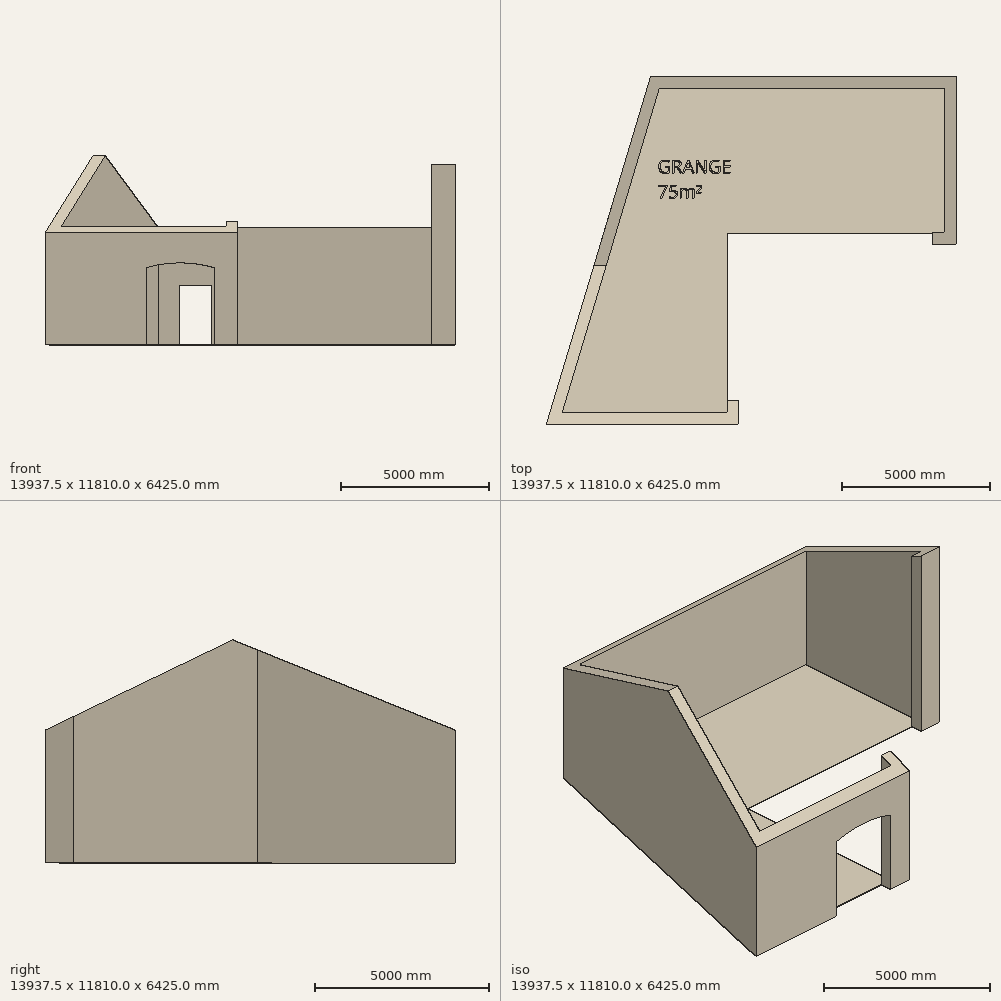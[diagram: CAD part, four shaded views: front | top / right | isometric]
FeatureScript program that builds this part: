
annotation { "Feature Type Name" : "Feature", "Feature Type Description" : "" }
export const myFeature = defineFeature(function(context is Context, id is Id, definition is map)
    precondition{}
    {
        {
            var Q0;
            Q0=qCreatedBy(makeId("Top.planeOp"),FACE);
            var sketch = newSketch(context, id + "F0", { "sketchPlane" : qUnion([Q0])});
            skLineSegment(sketch, "E0", {"start": v(-9700, 4910) * mm, "end": v(0, 4910) * mm});
            skLineSegment(sketch, "E1", {"start": v(-9700, 4910) * mm, "end": v(-13000, -6100) * mm});
            skLineSegment(sketch, "E2", {"start": v(0, 4910) * mm, "end": v(0, 0) * mm});
            skLineSegment(sketch, "E3", {"start": v(-7400, -6100) * mm, "end": v(-13000, -6100) * mm});
            skLineSegment(sketch, "E4.0", {"start": v(-9997.69, 5310) * mm, "end": v(400, 5310) * mm});
            skLineSegment(sketch, "E4.1", {"start": v(-7000, -6500) * mm, "end": v(-13537.47, -6500) * mm});
            skLineSegment(sketch, "E4.3", {"start": v(-9997.69, 5310) * mm, "end": v(-13537.47, -6500) * mm});
            skLineSegment(sketch, "E4.5", {"start": v(400, 5310) * mm, "end": v(400, -400) * mm});
            skLineSegment(sketch, "E5", {"start": v(-7400, -6100) * mm, "end": v(-7400, -5700) * mm});
            skLineSegment(sketch, "E6", {"start": v(-7400, -5700) * mm, "end": v(-7000, -5700) * mm});
            skLineSegment(sketch, "E7", {"start": v(-7000, -5700) * mm, "end": v(-7000, -6500) * mm});
            skLineSegment(sketch, "E8", {"start": v(0, 0) * mm, "end": v(-400, 0) * mm});
            skLineSegment(sketch, "E9", {"start": v(-400, 0) * mm, "end": v(-400, -400) * mm});
            skLineSegment(sketch, "E10", {"start": v(-400, -400) * mm, "end": v(400, -400) * mm});
            skSolve(sketch);
        }
        {
            var Q0;
            Q0 = qSketchRegion(id + "F0", true);
            extrude(context, id + "F1", {"entities" : qUnion([Q0]), "depth" : 6400 * mm});
        }
        {
            var Q0;
            Q0=qCreatedBy(makeId("Right.planeOp"),FACE);
            var sketch = newSketch(context, id + "F2", { "sketchPlane" : qUnion([Q0])});
            skLineSegment(sketch, "E11", {"start": v(-6500, 3800) * mm, "end": v(-1100, 6400) * mm});
            skLineSegment(sketch, "E12", {"start": v(-1100, 6400) * mm, "end": v(5310, 3800) * mm});
            skLineSegment(sketch, "E13", {"start": v(5310, 3800) * mm, "end": v(5310, 0) * mm});
            skLineSegment(sketch, "E14", {"start": v(5310, 3800) * mm, "end": v(5310, 6400) * mm});
            skLineSegment(sketch, "E15", {"start": v(-6500, 6400) * mm, "end": v(5310, 6400) * mm});
            skLineSegment(sketch, "E16", {"start": v(-6500, 6400) * mm, "end": v(-6500, 3800) * mm});
            skSolve(sketch);
        }
        {
            var Q0;
            Q0 = qSketchRegion(id + "F2", true);
            extrude(context, id + "F3", {"entities" : qUnion([Q0]), "operationType" : NewBodyOperationType.REMOVE, "endBound" : BoundingType.THROUGH_ALL, "depth" : 25.4 * mm, "hasSecondDirection" : true, "secondDirectionBound" : BoundingType.THROUGH_ALL, "secondDirectionOppositeDirection" : true, "secondDirectionDepth" : 25.4 * mm});
        }
        {
            var Q0;
            Q0=makeQuery(id+"F1.opExtrude","SWEPT_FACE",FACE,{"disambiguationData":[OSD([sQuery(id+"F0.wireOp",EDGE,"E4.0")])]});
            var sketch = newSketch(context, id + "F4", { "sketchPlane" : qUnion([Q0])});
            skLineSegment(sketch, "E17.bottom", {"start": v(7897.69, 0) * mm, "end": v(8997.69, 0) * mm});
            skLineSegment(sketch, "E17.top", {"start": v(7897.69, 2000) * mm, "end": v(8997.69, 2000) * mm});
            skLineSegment(sketch, "E17.left", {"start": v(7897.69, 0) * mm, "end": v(7897.69, 2000) * mm});
            skLineSegment(sketch, "E17.right", {"start": v(8997.69, 0) * mm, "end": v(8997.69, 2000) * mm});
            skSolve(sketch);
        }
        {
            var Q0;
            Q0 = qSketchRegion(id + "F4", true);
            extrude(context, id + "F5", {"entities" : qUnion([Q0]), "operationType" : NewBodyOperationType.REMOVE, "endBound" : BoundingType.UP_TO_NEXT, "oppositeDirection" : true, "depth" : 25.4 * mm});
        }
        {
            var Q0;
            Q0=makeQuery(id+"F1.opExtrude","SWEPT_FACE",FACE,{"disambiguationData":[OSD([sQuery(id+"F0.wireOp",EDGE,"E4.1")])]});
            var sketch = newSketch(context, id + "F6", { "sketchPlane" : qUnion([Q0])});
            skLineSegment(sketch, "E18", {"start": v(-10100, 0) * mm, "end": v(-10100, 2600) * mm});
            skArc(sketch, "E19", {"start": v(-7800, 2600) * mm, "mid": v(-8950, 2768.88) * mm, "end": v(-10100, 2600) * mm});
            skLineSegment(sketch, "E20", {"start": v(-7800, 2600) * mm, "end": v(-7800, 0) * mm});
            skLineSegment(sketch, "E21", {"start": v(-7800, 0) * mm, "end": v(-10100, 0) * mm});
            skSolve(sketch);
        }
        {
            var Q0;
            Q0 = qSketchRegion(id + "F6", true);
            extrude(context, id + "F7", {"entities" : qUnion([Q0]), "operationType" : NewBodyOperationType.REMOVE, "endBound" : BoundingType.UP_TO_NEXT, "oppositeDirection" : true, "depth" : 25.4 * mm});
        }
        {
            var Q0;
            {var subQ0=sQuery(id+"F0.wireOp",EDGE,"E3");var subQ1=sQuery(id+"F0.wireOp",EDGE,"E4.0");var subQ2=sQuery(id+"F0.wireOp",EDGE,"E1");var subQ3=sQuery(id+"F0.wireOp",EDGE,"E0");var subQ4=sQuery(id+"F0.wireOp",EDGE,"E4.3");var subQ5=sQuery(id+"F0.wireOp",EDGE,"E4.1");Q0=makeQuery(id+"F7.boolean.opBoolean","SPLIT",FACE,{"disambiguationData":[TD([makeQuery(id+"F1.opExtrude","SWEPT_FACE",FACE,{"disambiguationData":[OSD([subQ2])]})])],"derivedFrom":makeQuery(id+"F1.opExtrude","CAP_FACE",FACE,{"disambiguationData":[OSD([subQ3,subQ2,sQuery(id+"F0.wireOp",EDGE,"E2"),sQuery(id+"F0.wireOp",EDGE,"q86xWEi4-8NHh-2lQc-s4JO-oboVVbpXyoTF"),sQuery(id+"F0.wireOp",EDGE,"fW7YdV6a-fR6s-xuWl-E4J9-OQ2L1WpyIvuU"),subQ0,subQ1,subQ5,sQuery(id+"F0.wireOp",EDGE,"E4.2"),subQ4,sQuery(id+"F0.wireOp",EDGE,"E4.4"),sQuery(id+"F0.wireOp",EDGE,"E4.5")])],"isStart":true})});}
            var sketch = newSketch(context, id + "F8", { "sketchPlane" : qUnion([Q0])});
            skLineSegment(sketch, "E22", {"start": v(-9997.69, -5310) * mm, "end": v(400, -5310) * mm});
            skLineSegment(sketch, "E23", {"start": v(400, -5310) * mm, "end": v(400, -5310) * mm});
            skLineSegment(sketch, "E24", {"start": v(-13417.58, 6100) * mm, "end": v(-9997.69, -5310) * mm});
            skLineSegment(sketch, "E25", {"start": v(400, -5310) * mm, "end": v(400, 0) * mm});
            skLineSegment(sketch, "E26", {"start": v(400, 0) * mm, "end": v(-7400, 0) * mm});
            skLineSegment(sketch, "E27", {"start": v(-7400, 0) * mm, "end": v(-7400, 6100) * mm});
            skLineSegment(sketch, "E28", {"start": v(-7400, 6100) * mm, "end": v(-13417.58, 6100) * mm});
            skSolve(sketch);
        }
        {
            var Q0;
            Q0 = qSketchRegion(id + "F8", true);
            extrude(context, id + "F9", {"entities" : qUnion([Q0]), "operationType" : NewBodyOperationType.ADD, "oppositeDirection" : true, "depth" : 1 * mm, "hasSecondDirection" : true, "secondDirectionOppositeDirection" : false, "secondDirectionDepth" : 25 * mm});
        }
        {
            var Q0;
            Q0=makeQuery(id+"F9.opExtrude","CAP_FACE",FACE,{"disambiguationData":[OSD([sQuery(id+"F8.wireOp",EDGE,"E22"),sQuery(id+"F8.wireOp",EDGE,"E24"),sQuery(id+"F8.wireOp",EDGE,"E25"),sQuery(id+"F8.wireOp",EDGE,"E26"),sQuery(id+"F8.wireOp",EDGE,"E27"),sQuery(id+"F8.wireOp",EDGE,"E28")])],"isStart":false});
            var sketch = newSketch(context, id + "F10", { "sketchPlane" : qUnion([Q0])});
            skText(sketch, "E29", { "text": "GRANGE\n75m²", "fontName": "OpenSans-Regular.ttf"});
            const initialGuessF10  = {"E29": [-9.75796, 2.02622, 1, 0, 0.45193]};
            skSetInitialGuess(sketch, initialGuessF10);
            skSolve(sketch);
        }
        {
            var Q0;
            Q0 = qSketchRegion(id + "F10", true);
            extrude(context, id + "F11", {"entities" : qUnion([Q0]), "operationType" : NewBodyOperationType.REMOVE, "oppositeDirection" : true, "depth" : 25 * mm});
        }
    });
